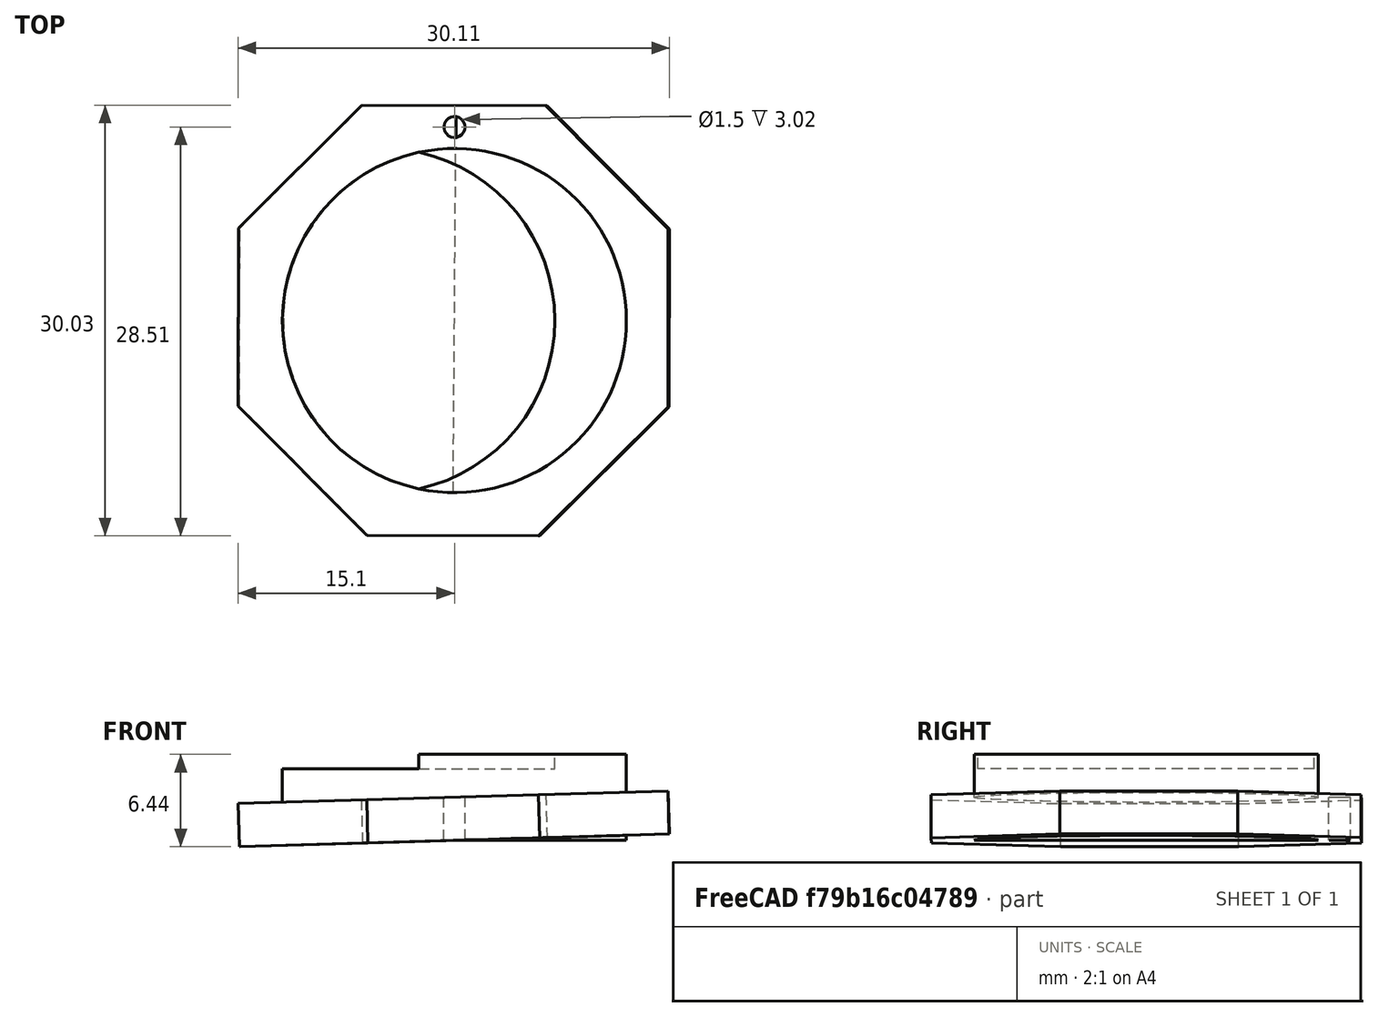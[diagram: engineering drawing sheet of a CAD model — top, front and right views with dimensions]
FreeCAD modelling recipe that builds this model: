
FCSTD DOCUMENT  (FreeCAD 0.16R6712 (Git))
Label: Lavero
License: All rights reserved
LicenseURL: http://en.wikipedia.org/wiki/All_rights_reserved
objects: Part::Cylinder×4, Part::Box×2, Part::Cut×2, Part::Common×1, Part::MultiFuse×1
note: 10 computed .brp shape members not serialized (recipe doc carries the construction recipe); baked Part::Feature solids carry a one-line shape summary decoded from their .brp

FEATURE [Part::Box] Box  label="Cubo"
  Height = 3
  Length = 30
  Placement = pos=(-15,-15,0) rot=(0,0,1;0rad)
  Width = 30
FEATURE [Part::Box] Box001  label="Cubo001"
  Height = 3
  Length = 30
  Placement = pos=(0,-21,0) rot=(0,0,1;0.785398rad)
  Width = 30
FEATURE [Part::Common] Common
  Base = -> Box
  Placement = pos=(0,0,0) rot=(-0.006487,-0.996503,-0.083305;0.029231rad)
  Tool = -> Box001
FEATURE [Part::Cylinder] Cylinder  label="Cilindro"
  Angle = 360
  Height = 5
  Radius = 12
FEATURE [Part::Cylinder] Cylinder001  label="Cilindro001"
  Angle = 360
  Height = 6
  Placement = pos=(30,0,0) rot=(0,0,1;0rad)
  Radius = 12
FEATURE [Part::Cylinder] Cylinder002  label="Cilindro002"
  Angle = 360
  Height = 10
  Placement = pos=(25,0,0) rot=(0,0,1;0rad)
  Radius = 12
FEATURE [Part::Cut] Cut  label="Luna"
  Base = -> Cylinder001
  Placement = pos=(-30,0,0) rot=(0,0,1;0rad)
  Tool = -> Cylinder002
FEATURE [Part::MultiFuse] Fusion
  Shapes = -> [Common,Cylinder,Cut]
FEATURE [Part::Cylinder] Cylinder003  label="Agujero"
  Angle = 360
  Height = 10
  Placement = pos=(0,13.5,0) rot=(0,0,1;0rad)
  Radius = 0.75
FEATURE [Part::Cut] Cut001  label="Llavero"
  Base = -> Fusion
  Tool = -> Cylinder003
